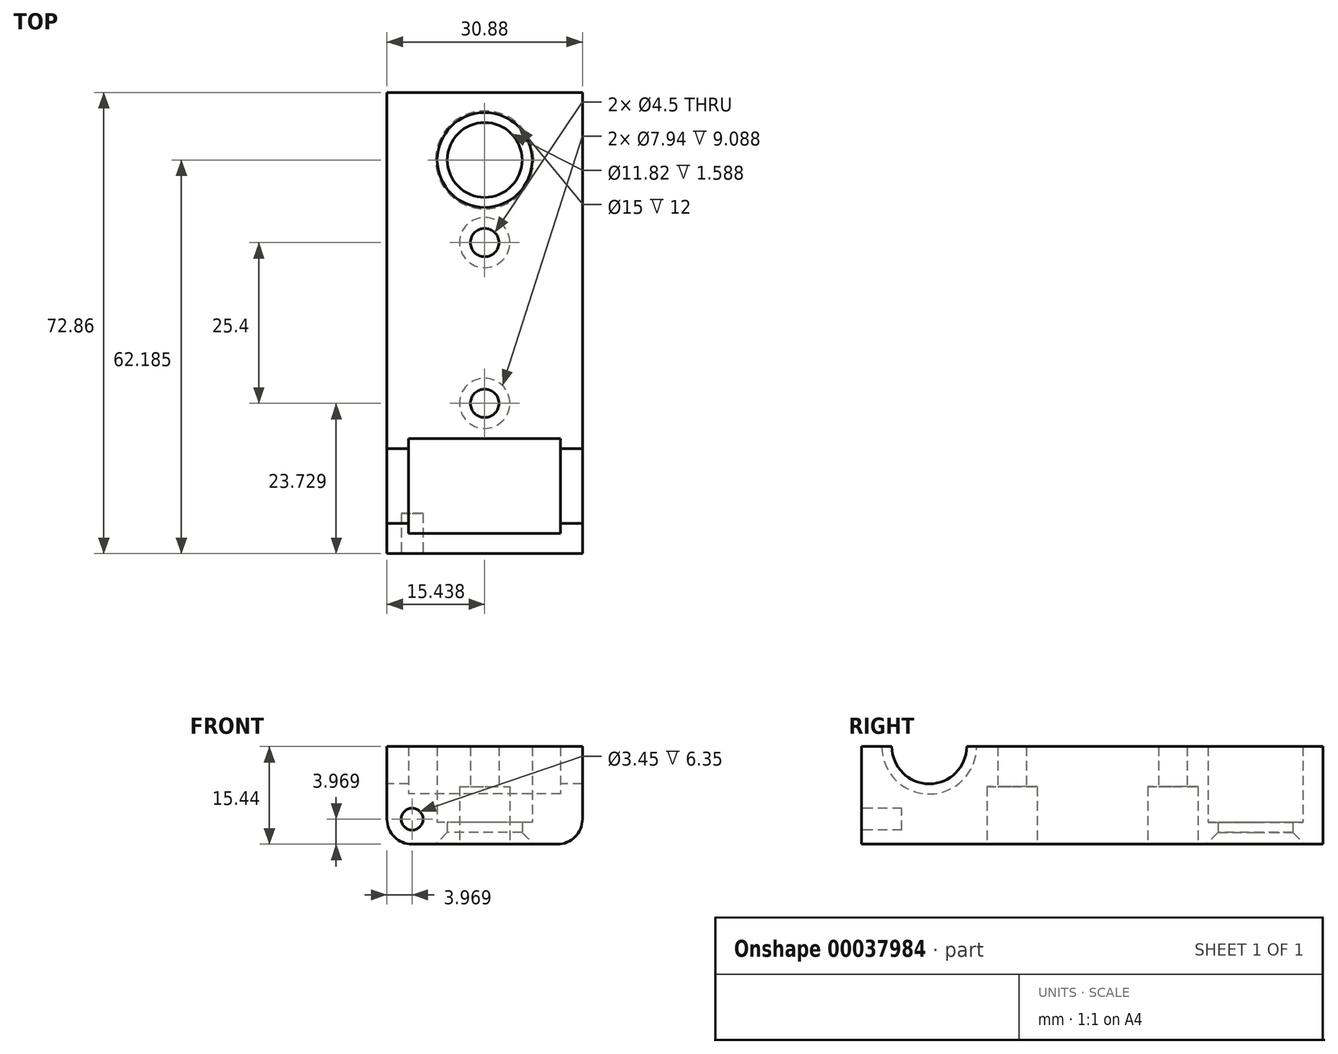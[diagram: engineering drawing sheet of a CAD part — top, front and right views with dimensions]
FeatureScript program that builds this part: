
annotation { "Feature Type Name" : "Feature", "Feature Type Description" : "" }
export const myFeature = defineFeature(function(context is Context, id is Id, definition is map)
    precondition{}
    {
        {
            var Q0;
            Q0=qCreatedBy(makeId("Top.planeOp"),FACE);
            var sketch = newSketch(context, id + "F0", { "sketchPlane" : qUnion([Q0])});
            skLineSegment(sketch, "E0.bottom", {"start": v(0, 0) * mm, "end": v(30.88, 0) * mm});
            skLineSegment(sketch, "E0.top", {"start": v(0, -72.86) * mm, "end": v(30.88, -72.86) * mm});
            skLineSegment(sketch, "E0.left", {"start": v(0, 0) * mm, "end": v(0, -72.86) * mm});
            skLineSegment(sketch, "E0.right", {"start": v(30.88, 0) * mm, "end": v(30.88, -72.86) * mm});
            skLineSegment(sketch, "E1", {"start": v(15.44, 0) * mm, "end": v(15.44, -10.67) * mm, "construction": true});
            skCircle(sketch, "E2", {"center": v(15.44, -10.67) * mm, "radius": 5.91 * mm});
            skLineSegment(sketch, "E3", {"start": v(15.44, -10.67) * mm, "end": v(15.44, -23.73) * mm, "construction": true});
            skLineSegment(sketch, "E4", {"start": v(15.44, -23.73) * mm, "end": v(15.44, -49.13) * mm, "construction": true});
            skCircle(sketch, "E5", {"center": v(15.44, -10.67) * mm, "radius": 7.5 * mm, "construction": true});
            skLineSegment(sketch, "E6", {"start": v(15.44, -49.13) * mm, "end": v(15.44, -72.86) * mm, "construction": true});
            skCircle(sketch, "E7", {"center": v(15.44, -23.73) * mm, "radius": 2.25 * mm});
            skCircle(sketch, "E8", {"center": v(15.44, -49.13) * mm, "radius": 2.25 * mm});
            skSolve(sketch);
        }
        {
            var Q0;
            Q0=qSketchRegion(id+"F0",true);
            extrude(context, id + "F1", {"entities" : qUnion([Q0]), "depth" : 3.44 * mm});
        }
        {
            var Q0;
            Q0=makeQuery(id+"F1.opExtrude","CAP_FACE",FACE,{"disambiguationData":[OSD([sQuery(id+"F0.wireOp",EDGE,"E0.bottom"),sQuery(id+"F0.wireOp",EDGE,"E0.top"),sQuery(id+"F0.wireOp",EDGE,"E0.left"),sQuery(id+"F0.wireOp",EDGE,"E0.right"),sQuery(id+"F0.wireOp",EDGE,"E2"),sQuery(id+"F0.wireOp",EDGE,"E7"),sQuery(id+"F0.wireOp",EDGE,"E8")])],"isStart":false});
            var sketch = newSketch(context, id + "F2", { "sketchPlane" : qUnion([Q0])});
            skCircle(sketch, "E9", {"center": v(15.44, -10.67) * mm, "radius": 7.5 * mm});
            skSolve(sketch);
        }
        {
            var Q0;
            Q0=makeQuery(id+"F2.imprint","IMPRINT",FACE,{"disambiguationData":[TD([[makeQuery(id+"F2.imprint","IMPRINT",EDGE,{"derivedFrom":sQuery(id+"F2.wireOp",EDGE,"E9")}),-1.0]])]});
            extrude(context, id + "F3", {"entities" : qUnion([Q0]), "operationType" : NewBodyOperationType.ADD, "depth" : 12 * mm});
        }
        {
            var Q0;
            Q0=makeQuery(id+"F3.opExtrude","CAP_FACE",FACE,{"disambiguationData":[OSD([sQuery(id+"F0.wireOp",EDGE,"E0.bottom"),sQuery(id+"F0.wireOp",EDGE,"E0.top"),sQuery(id+"F0.wireOp",EDGE,"E0.left"),sQuery(id+"F0.wireOp",EDGE,"E0.right"),sQuery(id+"F0.wireOp",EDGE,"E7"),sQuery(id+"F0.wireOp",EDGE,"E8"),sQuery(id+"F2.wireOp",EDGE,"E9")])],"isStart":false});
            var sketch = newSketch(context, id + "F4", { "sketchPlane" : qUnion([Q0])});
            skLineSegment(sketch, "E10.bottom", {"start": v(3.44, -69.69) * mm, "end": v(27.44, -69.69) * mm});
            skLineSegment(sketch, "E10.top", {"start": v(3.44, -54.69) * mm, "end": v(27.44, -54.69) * mm});
            skLineSegment(sketch, "E10.left", {"start": v(3.44, -69.69) * mm, "end": v(3.44, -54.69) * mm});
            skLineSegment(sketch, "E10.right", {"start": v(27.44, -69.69) * mm, "end": v(27.44, -54.69) * mm});
            skLineSegment(sketch, "E11", {"start": v(15.44, -69.69) * mm, "end": v(15.44, -72.86) * mm, "construction": true});
            skSolve(sketch);
        }
        {
            var Q0;
            Q0=qSketchRegion(id+"F4",true);
            extrude(context, id + "F5", {"entities" : qUnion([Q0]), "operationType" : NewBodyOperationType.REMOVE, "oppositeDirection" : true, "depth" : 7.5 * mm});
        }
        {
            var Q0;
            Q0=makeQuery(id+"F5.boolean.opBoolean","COPY",EDGE,{"derivedFrom":makeQuery(id+"F5.opExtrude","CAP_EDGE",EDGE,{"disambiguationData":[OSD([sQuery(id+"F4.wireOp",EDGE,"E10.top")])],"isStart":false})});
            var Q1;
            Q1=makeQuery(id+"F5.boolean.opBoolean","COPY",EDGE,{"derivedFrom":makeQuery(id+"F5.opExtrude","CAP_EDGE",EDGE,{"disambiguationData":[OSD([sQuery(id+"F4.wireOp",EDGE,"E10.bottom")])],"isStart":false})});
            fillet(context, id + "F6", {"entities" : qUnion([Q0, Q1]), "radius" : 7.5 * mm, "tangentPropagation" : true, "allowEdgeOverflow" : false});
        }
        {
            var Q0;
            {var subQ0=sQuery(id+"F0.wireOp",EDGE,"E0.left");Q0=makeQuery(id+"F3.boolean.opBoolean","MERGE",FACE,{"derivedFrom":[makeQuery(id+"F1.opExtrude","SWEPT_FACE",FACE,{"disambiguationData":[OSD([subQ0])]}),makeQuery(id+"F3.opExtrude","SWEPT_FACE",FACE,{"disambiguationData":[OSD([subQ0])]})]});}
            var sketch = newSketch(context, id + "F7", { "sketchPlane" : qUnion([Q0])});
            skArc(sketch, "E12", {"start": v(56.28, 15.44) * mm, "mid": v(62.19, 9.53) * mm, "end": v(68.1, 15.44) * mm});
            skLineSegment(sketch, "E13", {"start": v(56.28, 15.44) * mm, "end": v(68.1, 15.44) * mm});
            skSolve(sketch);
        }
        {
            var Q0;
            Q0=qSketchRegion(id+"F7",true);
            var Q1;
            {var subQ0=sQuery(id+"F0.wireOp",EDGE,"E0.right");Q1=makeQuery(id+"F3.boolean.opBoolean","MERGE",FACE,{"derivedFrom":[makeQuery(id+"F1.opExtrude","SWEPT_FACE",FACE,{"disambiguationData":[OSD([subQ0])]}),makeQuery(id+"F3.opExtrude","SWEPT_FACE",FACE,{"disambiguationData":[OSD([subQ0])]})]});}
            extrude(context, id + "F8", {"entities" : qUnion([Q0]), "operationType" : NewBodyOperationType.REMOVE, "endBound" : BoundingType.UP_TO_SURFACE, "oppositeDirection" : true, "endBoundEntityFace" : qUnion([Q1]), "depth" : 25.4 * mm});
        }
        {
            var Q0;
            Q0=makeQuery(id+"F1.opExtrude","CAP_FACE",FACE,{"disambiguationData":[OSD([sQuery(id+"F0.wireOp",EDGE,"E0.bottom"),sQuery(id+"F0.wireOp",EDGE,"E0.top"),sQuery(id+"F0.wireOp",EDGE,"E0.left"),sQuery(id+"F0.wireOp",EDGE,"E0.right"),sQuery(id+"F0.wireOp",EDGE,"E2"),sQuery(id+"F0.wireOp",EDGE,"E7"),sQuery(id+"F0.wireOp",EDGE,"E8")])],"isStart":true});
            var sketch = newSketch(context, id + "F9", { "sketchPlane" : qUnion([Q0])});
            skCircle(sketch, "E14", {"center": v(15.44, 23.73) * mm, "radius": 3.97 * mm});
            skCircle(sketch, "E15", {"center": v(15.44, 49.13) * mm, "radius": 3.97 * mm});
            skSolve(sketch);
        }
        {
            var Q0;
            Q0=qSketchRegion(id+"F9",true);
            extrude(context, id + "F10", {"entities" : qUnion([Q0]), "operationType" : NewBodyOperationType.REMOVE, "oppositeDirection" : true, "depth" : 9.1 * mm});
        }
        {
            var Q0;
            Q0=makeQuery(id+"F1.opExtrude","CAP_EDGE",EDGE,{"disambiguationData":[OSD([sQuery(id+"F0.wireOp",EDGE,"E0.left")])],"isStart":true});
            var Q1;
            Q1=makeQuery(id+"F1.opExtrude","CAP_EDGE",EDGE,{"disambiguationData":[OSD([sQuery(id+"F0.wireOp",EDGE,"E0.right")])],"isStart":true});
            fillet(context, id + "F11", {"entities" : qUnion([Q0, Q1]), "radius" : 3.97 * mm, "tangentPropagation" : true, "allowEdgeOverflow" : false});
        }
        {
            var Q0;
            {var subQ0=sQuery(id+"F0.wireOp",EDGE,"E0.top");Q0=makeQuery(id+"F3.boolean.opBoolean","MERGE",FACE,{"derivedFrom":[makeQuery(id+"F1.opExtrude","SWEPT_FACE",FACE,{"disambiguationData":[OSD([subQ0])]}),makeQuery(id+"F3.opExtrude","SWEPT_FACE",FACE,{"disambiguationData":[OSD([subQ0])]})]});}
            var sketch = newSketch(context, id + "F12", { "sketchPlane" : qUnion([Q0])});
            skCircle(sketch, "E16", {"center": v(3.97, 3.97) * mm, "radius": 1.73 * mm});
            skSolve(sketch);
        }
        {
            var Q0;
            Q0=qSketchRegion(id+"F12",true);
            extrude(context, id + "F13", {"entities" : qUnion([Q0]), "operationType" : NewBodyOperationType.REMOVE, "oppositeDirection" : true, "depth" : 6.35 * mm});
        }
        {
            var Q0;
            Q0=makeQuery(id+"F1.opExtrude","CAP_EDGE",EDGE,{"disambiguationData":[OSD([sQuery(id+"F0.wireOp",EDGE,"E2")])],"isStart":true});
            var Q1;
            Q1=makeQuery(id+"F8.boolean.opBoolean","COPY",EDGE,{"derivedFrom":makeQuery(id+"F8.opExtrude","CAP_EDGE",EDGE,{"disambiguationData":[OSD([sQuery(id+"F7.wireOp",EDGE,"E12")])],"isStart":false})});
            var Q2;
            Q2=makeQuery(id+"F8.boolean.opBoolean","COPY",EDGE,{"derivedFrom":makeQuery(id+"F8.opExtrude","CAP_EDGE",EDGE,{"disambiguationData":[OSD([sQuery(id+"F7.wireOp",EDGE,"E12")])],"isStart":true})});
            chamfer(context, id + "F14", {"entities" : qUnion([Q0, Q1, Q2]), "width" : 1.85 * mm, "tangentPropagation" : true});
        }
    });
